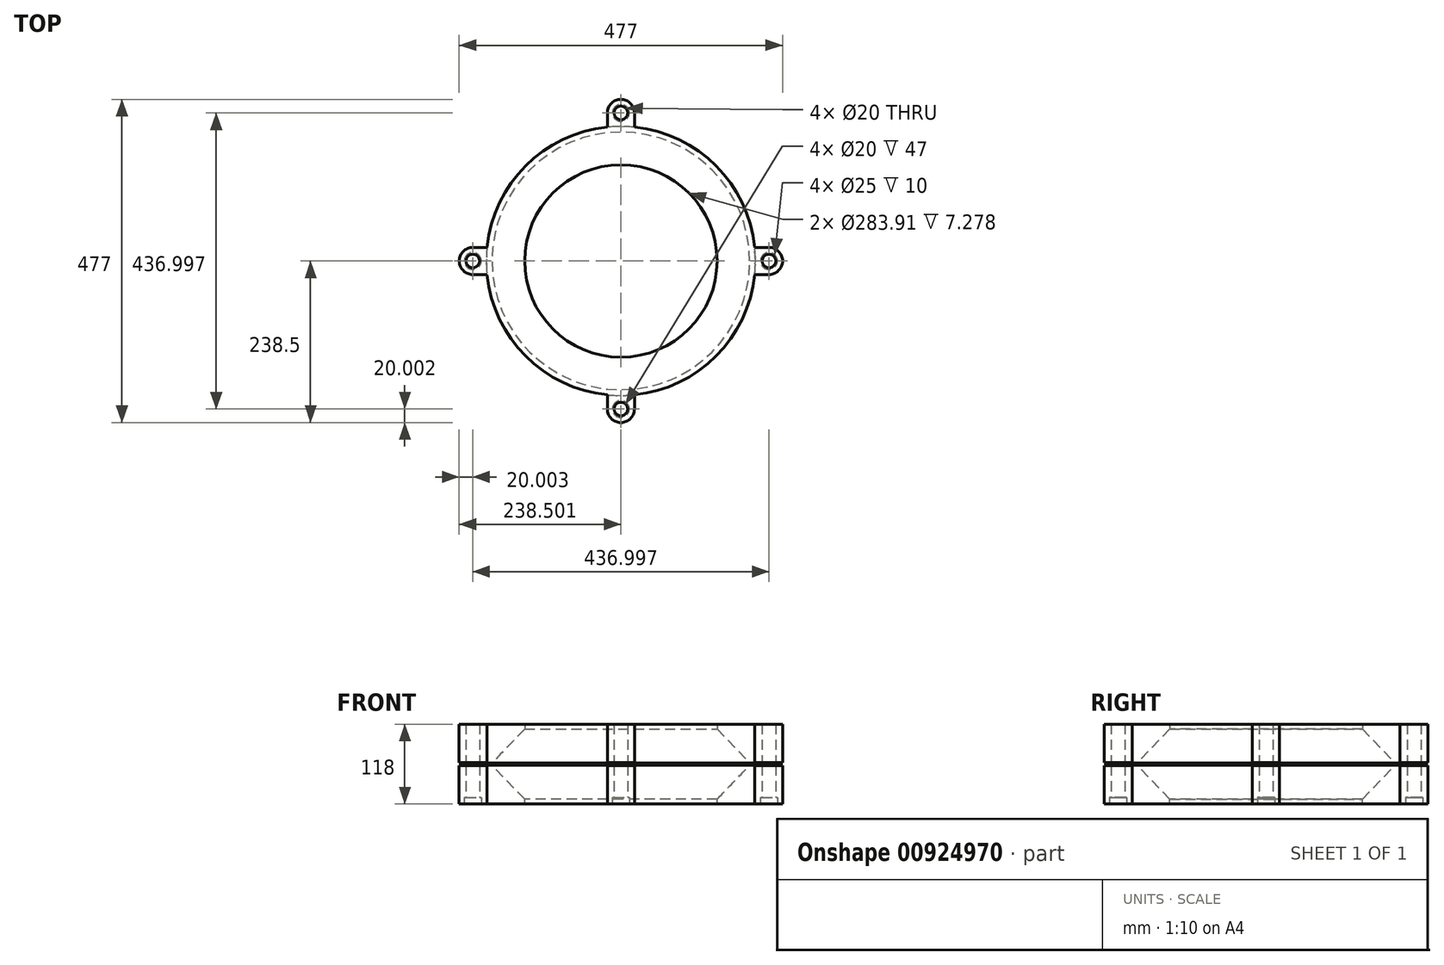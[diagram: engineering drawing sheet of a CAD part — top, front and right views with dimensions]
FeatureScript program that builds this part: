
annotation { "Feature Type Name" : "Feature", "Feature Type Description" : "" }
export const myFeature = defineFeature(function(context is Context, id is Id, definition is map)
    precondition{}
    {
        {
            var Q0;
            Q0=qCreatedBy(makeId("Front.planeOp"),FACE);
            var sketch = newSketch(context, id + "F0", { "sketchPlane" : qUnion([Q0])});
            skLineSegment(sketch, "E0", {"start": v(-122.7, 61.49) * mm, "end": v(-122.7, 4.01) * mm});
            skLineSegment(sketch, "E1", {"start": v(-122.7, 4.01) * mm, "end": v(-66.15, 4.01) * mm});
            skLineSegment(sketch, "E2", {"start": v(-66.15, 4.01) * mm, "end": v(-66.15, 11.29) * mm});
            skLineSegment(sketch, "E3", {"start": v(-66.15, 11.29) * mm, "end": v(-114.3, 61.49) * mm});
            skLineSegment(sketch, "E4", {"start": v(-114.3, 61.49) * mm, "end": v(-122.7, 61.49) * mm});
            skLineSegment(sketch, "E5", {"start": v(-122.7, 61.67) * mm, "end": v(-114.3, 61.67) * mm});
            skLineSegment(sketch, "E6.MirrorCS", {"start": v(-114.3, 61.84) * mm, "end": v(-122.7, 61.84) * mm});
            skLineSegment(sketch, "E7.MirrorCS", {"start": v(-122.7, 61.84) * mm, "end": v(-122.7, 119.32) * mm});
            skLineSegment(sketch, "E8.MirrorCS", {"start": v(-66.15, 112.04) * mm, "end": v(-114.3, 61.84) * mm});
            skLineSegment(sketch, "E9.MirrorCS", {"start": v(-122.7, 119.32) * mm, "end": v(-66.15, 119.32) * mm});
            skLineSegment(sketch, "E10.MirrorCS", {"start": v(-66.15, 119.32) * mm, "end": v(-66.15, 112.04) * mm});
            skLineSegment(sketch, "E11", {"start": v(75.8, 4.01) * mm, "end": v(75.8, 119.32) * mm});
            skSolve(sketch);
        }
        {
            var Q0;
            Q0=makeQuery(id+"F0.imprint","IMPRINT",FACE,{"disambiguationData":[TD([[makeQuery(id+"F0.imprint","IMPRINT",EDGE,{"derivedFrom":sQuery(id+"F0.wireOp",EDGE,"E6.MirrorCS")}),-1.0]])]});
            var Q1;
            Q1=makeQuery(id+"F0.imprint","IMPRINT",FACE,{"disambiguationData":[TD([[makeQuery(id+"F0.imprint","IMPRINT",EDGE,{"derivedFrom":sQuery(id+"F0.wireOp",EDGE,"E0")}),1.0]])]});
            var Q2;
            Q2=sQuery(id+"F0.wireOp",EDGE,"E11");
            revolve(context, id + "F1", {"surfaceOperationType" : NewSurfaceOperationType.NEW, "entities" : qUnion([Q0, Q1]), "axis" : qUnion([Q2]), "revolveType" : RevolveType.FULL});
        }
        {
            var Q0;
            Q0=makeQuery(id+"F1.opRevolve","SWEPT_FACE",FACE,{"disambiguationData":[OSD([sQuery(id+"F0.wireOp",EDGE,"E9.MirrorCS")])]});
            var sketch = newSketch(context, id + "F2", { "sketchPlane" : qUnion([Q0])});
            skLineSegment(sketch, "E12", {"start": v(75.8, 0) * mm, "end": v(75.8, 198.5) * mm});
            skLineSegment(sketch, "E13", {"start": v(75.8, 0) * mm, "end": v(274.3, 0) * mm});
            skLineSegment(sketch, "E14", {"start": v(75.8, 198.5) * mm, "end": v(75.8, 238.5) * mm});
            skLineSegment(sketch, "E15", {"start": v(274.3, 0) * mm, "end": v(314.3, 0) * mm});
            skLineSegment(sketch, "E16", {"start": v(75.8, 0) * mm, "end": v(75.8, -238.5) * mm});
            skLineSegment(sketch, "E17", {"start": v(75.8, 0) * mm, "end": v(-162.7, 0) * mm});
            skLineSegment(sketch, "E18.bottom", {"start": v(55.8, 238.5) * mm, "end": v(75.8, 238.5) * mm});
            skLineSegment(sketch, "E18.top", {"start": v(55.8, -238.5) * mm, "end": v(75.8, -238.5) * mm});
            skLineSegment(sketch, "E18.left", {"start": v(55.8, 238.5) * mm, "end": v(55.8, -238.5) * mm});
            skLineSegment(sketch, "E18.right", {"start": v(75.8, 238.5) * mm, "end": v(75.8, -238.5) * mm});
            skLineSegment(sketch, "E19.bottom", {"start": v(75.8, 238.5) * mm, "end": v(95.8, 238.5) * mm});
            skLineSegment(sketch, "E19.top", {"start": v(75.8, -238.5) * mm, "end": v(95.8, -238.5) * mm});
            skLineSegment(sketch, "E19.right", {"start": v(95.8, 238.5) * mm, "end": v(95.8, -238.5) * mm});
            skLineSegment(sketch, "E20.bottom", {"start": v(-162.7, 0) * mm, "end": v(314.3, 0) * mm});
            skLineSegment(sketch, "E20.top", {"start": v(-162.7, 20) * mm, "end": v(314.3, 20) * mm});
            skLineSegment(sketch, "E20.left", {"start": v(-162.7, 0) * mm, "end": v(-162.7, 20) * mm});
            skLineSegment(sketch, "E20.right", {"start": v(314.3, 0) * mm, "end": v(314.3, 20) * mm});
            skLineSegment(sketch, "E21.top", {"start": v(-162.7, -20) * mm, "end": v(314.3, -20) * mm});
            skLineSegment(sketch, "E21.left", {"start": v(-162.7, 0) * mm, "end": v(-162.7, -20) * mm});
            skLineSegment(sketch, "E21.right", {"start": v(314.3, 0) * mm, "end": v(314.3, -20) * mm});
            skSolve(sketch);
        }
        {
            var Q0;
            {var subQ0=sQuery(id+"F2.wireOp",EDGE,"E21.left");Q0=makeQuery(id+"F2.imprint","IMPRINT",FACE,{"disambiguationData":[TD([[makeQuery(id+"F2.imprint","IMPRINT",EDGE,{"derivedFrom":subQ0}),1.0]])]});}
            var Q1;
            {var subQ0=sQuery(id+"F2.wireOp",EDGE,"E20.left");Q1=makeQuery(id+"F2.imprint","IMPRINT",FACE,{"disambiguationData":[TD([[makeQuery(id+"F2.imprint","IMPRINT",EDGE,{"derivedFrom":subQ0}),-1.0]])]});}
            var Q2;
            {var subQ0=sQuery(id+"F2.wireOp",EDGE,"E18.bottom");Q2=makeQuery(id+"F2.imprint","IMPRINT",FACE,{"disambiguationData":[TD([[makeQuery(id+"F2.imprint","IMPRINT",EDGE,{"derivedFrom":subQ0}),-1.0]])]});}
            var Q3;
            {var subQ0=sQuery(id+"F2.wireOp",EDGE,"E19.bottom");Q3=makeQuery(id+"F2.imprint","IMPRINT",FACE,{"disambiguationData":[TD([[makeQuery(id+"F2.imprint","IMPRINT",EDGE,{"derivedFrom":subQ0}),-1.0]])]});}
            var Q4;
            {var subQ0=sQuery(id+"F2.wireOp",EDGE,"E18.top");Q4=makeQuery(id+"F2.imprint","IMPRINT",FACE,{"disambiguationData":[TD([[makeQuery(id+"F2.imprint","IMPRINT",EDGE,{"derivedFrom":subQ0}),1.0]])]});}
            var Q5;
            {var subQ0=sQuery(id+"F2.wireOp",EDGE,"E19.top");Q5=makeQuery(id+"F2.imprint","IMPRINT",FACE,{"disambiguationData":[TD([[makeQuery(id+"F2.imprint","IMPRINT",EDGE,{"derivedFrom":subQ0}),1.0]])]});}
            var Q6;
            {var subQ0=sQuery(id+"F2.wireOp",EDGE,"E21.right");Q6=makeQuery(id+"F2.imprint","IMPRINT",FACE,{"disambiguationData":[TD([[makeQuery(id+"F2.imprint","IMPRINT",EDGE,{"derivedFrom":subQ0}),-1.0]])]});}
            var Q7;
            {var subQ0=sQuery(id+"F2.wireOp",EDGE,"E20.right");Q7=makeQuery(id+"F2.imprint","IMPRINT",FACE,{"disambiguationData":[TD([[makeQuery(id+"F2.imprint","IMPRINT",EDGE,{"derivedFrom":subQ0}),1.0]])]});}
            extrude(context, id + "F3", {"entities" : qUnion([Q0, Q1, Q2, Q3, Q4, Q5, Q6, Q7]), "operationType" : NewBodyOperationType.ADD, "oppositeDirection" : true, "depth" : 57 * mm, "offsetDistance" : 25 * mm});
        }
        {
            var Q0;
            {var subQ0=sQuery(id+"F2.wireOp",EDGE,"E19.right");var subQ1=sQuery(id+"F0.wireOp",EDGE,"E9.MirrorCS");var subQ2=sQuery(id+"F0.wireOp",EDGE,"E7.MirrorCS");Q0=makeQuery(id+"F3.opExtrude","SWEPT_EDGE",EDGE,{"disambiguationData":[OSD([subQ2,subQ1,subQ0]),TDD([makeQuery(id+"F2.imprint","INTERSECT",VERTEX,{"disambiguationData":[OD(1.0)],"derivedFrom":[makeQuery(id+"F1.opRevolve","SWEPT_EDGE",EDGE,{"disambiguationData":[OSD([subQ2,subQ1])]}),subQ0]})])]});}
            var Q1;
            {var subQ0=sQuery(id+"F2.wireOp",EDGE,"E18.left");var subQ1=sQuery(id+"F0.wireOp",EDGE,"E9.MirrorCS");var subQ2=sQuery(id+"F0.wireOp",EDGE,"E7.MirrorCS");Q1=makeQuery(id+"F3.opExtrude","SWEPT_EDGE",EDGE,{"disambiguationData":[OSD([subQ2,subQ1,subQ0]),TDD([makeQuery(id+"F2.imprint","INTERSECT",VERTEX,{"disambiguationData":[OD(1.0)],"derivedFrom":[makeQuery(id+"F1.opRevolve","SWEPT_EDGE",EDGE,{"disambiguationData":[OSD([subQ2,subQ1])]}),subQ0]})])]});}
            var Q2;
            {var subQ0=sQuery(id+"F2.wireOp",EDGE,"E21.top");var subQ1=sQuery(id+"F0.wireOp",EDGE,"E9.MirrorCS");var subQ2=sQuery(id+"F0.wireOp",EDGE,"E7.MirrorCS");Q2=makeQuery(id+"F3.opExtrude","SWEPT_EDGE",EDGE,{"disambiguationData":[OSD([subQ2,subQ1,subQ0]),TDD([makeQuery(id+"F2.imprint","INTERSECT",VERTEX,{"disambiguationData":[OD(1.0)],"derivedFrom":[makeQuery(id+"F1.opRevolve","SWEPT_EDGE",EDGE,{"disambiguationData":[OSD([subQ2,subQ1])]}),subQ0]})])]});}
            var Q3;
            {var subQ0=sQuery(id+"F2.wireOp",EDGE,"E20.top");var subQ1=sQuery(id+"F0.wireOp",EDGE,"E9.MirrorCS");var subQ2=sQuery(id+"F0.wireOp",EDGE,"E7.MirrorCS");Q3=makeQuery(id+"F3.opExtrude","SWEPT_EDGE",EDGE,{"disambiguationData":[OSD([subQ2,subQ1,subQ0]),TDD([makeQuery(id+"F2.imprint","INTERSECT",VERTEX,{"disambiguationData":[OD(1.0)],"derivedFrom":[makeQuery(id+"F1.opRevolve","SWEPT_EDGE",EDGE,{"disambiguationData":[OSD([subQ2,subQ1])]}),subQ0]})])]});}
            var Q4;
            {var subQ0=sQuery(id+"F2.wireOp",EDGE,"E19.right");var subQ1=sQuery(id+"F0.wireOp",EDGE,"E9.MirrorCS");var subQ2=sQuery(id+"F0.wireOp",EDGE,"E7.MirrorCS");Q4=makeQuery(id+"F3.opExtrude","SWEPT_EDGE",EDGE,{"disambiguationData":[OSD([subQ2,subQ1,subQ0]),TDD([makeQuery(id+"F2.imprint","INTERSECT",VERTEX,{"disambiguationData":[OD(0.0)],"derivedFrom":[makeQuery(id+"F1.opRevolve","SWEPT_EDGE",EDGE,{"disambiguationData":[OSD([subQ2,subQ1])]}),subQ0]})])]});}
            var Q5;
            {var subQ0=sQuery(id+"F2.wireOp",EDGE,"E18.left");var subQ1=sQuery(id+"F0.wireOp",EDGE,"E9.MirrorCS");var subQ2=sQuery(id+"F0.wireOp",EDGE,"E7.MirrorCS");Q5=makeQuery(id+"F3.opExtrude","SWEPT_EDGE",EDGE,{"disambiguationData":[OSD([subQ2,subQ1,subQ0]),TDD([makeQuery(id+"F2.imprint","INTERSECT",VERTEX,{"disambiguationData":[OD(0.0)],"derivedFrom":[makeQuery(id+"F1.opRevolve","SWEPT_EDGE",EDGE,{"disambiguationData":[OSD([subQ2,subQ1])]}),subQ0]})])]});}
            var Q6;
            {var subQ0=sQuery(id+"F2.wireOp",EDGE,"E20.top");var subQ1=sQuery(id+"F0.wireOp",EDGE,"E9.MirrorCS");var subQ2=sQuery(id+"F0.wireOp",EDGE,"E7.MirrorCS");Q6=makeQuery(id+"F3.opExtrude","SWEPT_EDGE",EDGE,{"disambiguationData":[OSD([subQ2,subQ1,subQ0]),TDD([makeQuery(id+"F2.imprint","INTERSECT",VERTEX,{"disambiguationData":[OD(0.0)],"derivedFrom":[makeQuery(id+"F1.opRevolve","SWEPT_EDGE",EDGE,{"disambiguationData":[OSD([subQ2,subQ1])]}),subQ0]})])]});}
            var Q7;
            {var subQ0=sQuery(id+"F2.wireOp",EDGE,"E21.top");var subQ1=sQuery(id+"F0.wireOp",EDGE,"E9.MirrorCS");var subQ2=sQuery(id+"F0.wireOp",EDGE,"E7.MirrorCS");Q7=makeQuery(id+"F3.opExtrude","SWEPT_EDGE",EDGE,{"disambiguationData":[OSD([subQ2,subQ1,subQ0]),TDD([makeQuery(id+"F2.imprint","INTERSECT",VERTEX,{"disambiguationData":[OD(0.0)],"derivedFrom":[makeQuery(id+"F1.opRevolve","SWEPT_EDGE",EDGE,{"disambiguationData":[OSD([subQ2,subQ1])]}),subQ0]})])]});}
            var Q8;
            Q8=makeQuery(id+"F3.opExtrude","SWEPT_EDGE",EDGE,{"disambiguationData":[OSD([sQuery(id+"F2.wireOp",EDGE,"E21.top"),sQuery(id+"F2.wireOp",EDGE,"E21.left")])]});
            var Q9;
            Q9=makeQuery(id+"F3.opExtrude","SWEPT_EDGE",EDGE,{"disambiguationData":[OSD([sQuery(id+"F2.wireOp",EDGE,"E20.top"),sQuery(id+"F2.wireOp",EDGE,"E20.left")])]});
            var Q10;
            Q10=makeQuery(id+"F3.opExtrude","SWEPT_EDGE",EDGE,{"disambiguationData":[OSD([sQuery(id+"F2.wireOp",EDGE,"E18.bottom"),sQuery(id+"F2.wireOp",EDGE,"E18.left")])]});
            var Q11;
            Q11=makeQuery(id+"F3.opExtrude","SWEPT_EDGE",EDGE,{"disambiguationData":[OSD([sQuery(id+"F2.wireOp",EDGE,"E19.bottom"),sQuery(id+"F2.wireOp",EDGE,"E19.right")])]});
            var Q12;
            Q12=makeQuery(id+"F3.opExtrude","SWEPT_EDGE",EDGE,{"disambiguationData":[OSD([sQuery(id+"F2.wireOp",EDGE,"E20.top"),sQuery(id+"F2.wireOp",EDGE,"E20.right")])]});
            var Q13;
            Q13=makeQuery(id+"F3.opExtrude","SWEPT_EDGE",EDGE,{"disambiguationData":[OSD([sQuery(id+"F2.wireOp",EDGE,"E21.top"),sQuery(id+"F2.wireOp",EDGE,"E21.right")])]});
            var Q14;
            Q14=makeQuery(id+"F3.opExtrude","SWEPT_EDGE",EDGE,{"disambiguationData":[OSD([sQuery(id+"F2.wireOp",EDGE,"E19.top"),sQuery(id+"F2.wireOp",EDGE,"E19.right")])]});
            var Q15;
            Q15=makeQuery(id+"F3.opExtrude","SWEPT_EDGE",EDGE,{"disambiguationData":[OSD([sQuery(id+"F2.wireOp",EDGE,"E18.top"),sQuery(id+"F2.wireOp",EDGE,"E18.left")])]});
            fillet(context, id + "F4", {"entities" : qUnion([Q0, Q1, Q2, Q3, Q4, Q5, Q6, Q7, Q8, Q9, Q10, Q11, Q12, Q13, Q14, Q15]), "radius" : 20 * mm, "tangentPropagation" : true, "allowEdgeOverflow" : false});
        }
        {
            var Q0;
            Q0=makeQuery(id+"F1.opRevolve","SWEPT_BODY",BODY,{"disambiguationData":[OSD([sQuery(id+"F0.wireOp",EDGE,"E0"),sQuery(id+"F0.wireOp",EDGE,"E1"),sQuery(id+"F0.wireOp",EDGE,"E2"),sQuery(id+"F0.wireOp",EDGE,"E3"),sQuery(id+"F0.wireOp",EDGE,"E4")])]});
            deleteBodies(context, id + "F5", {"entities" : qUnion([Q0])});
        }
        {
            var Q0;
            Q0=makeQuery(id+"F1.opRevolve","SWEPT_BODY",BODY,{"disambiguationData":[OSD([sQuery(id+"F0.wireOp",EDGE,"E6.MirrorCS"),sQuery(id+"F0.wireOp",EDGE,"E7.MirrorCS"),sQuery(id+"F0.wireOp",EDGE,"E8.MirrorCS"),sQuery(id+"F0.wireOp",EDGE,"E9.MirrorCS"),sQuery(id+"F0.wireOp",EDGE,"E10.MirrorCS")])]});
            transform(context, id + "F6", {"entities" : qUnion([Q0]), "transformType" : TransformType.TRANSLATION_3D, "dx" : 0 * mm, "dy" : 0 * mm, "dz" : -59 * mm, "makeCopy" : true});
        }
        {
            var Q0;
            Q0=makeQuery(id+"F1.opRevolve","SWEPT_BODY",BODY,{"disambiguationData":[OSD([sQuery(id+"F0.wireOp",EDGE,"E6.MirrorCS"),sQuery(id+"F0.wireOp",EDGE,"E7.MirrorCS"),sQuery(id+"F0.wireOp",EDGE,"E8.MirrorCS"),sQuery(id+"F0.wireOp",EDGE,"E9.MirrorCS"),sQuery(id+"F0.wireOp",EDGE,"E10.MirrorCS")])]});
            var Q1;
            Q1=sQuery(id+"F2.wireOp",EDGE,"E18.right");
            transform(context, id + "F7", {"entities" : qUnion([Q0]), "transformType" : TransformType.ROTATION, "transformAxis" : qUnion([Q1]), "angle" : 180 * degree, "makeCopy" : false});
        }
        {
            var Q0;
            Q0=makeQuery(id+"F1.opRevolve","SWEPT_BODY",BODY,{"disambiguationData":[OSD([sQuery(id+"F0.wireOp",EDGE,"E6.MirrorCS"),sQuery(id+"F0.wireOp",EDGE,"E7.MirrorCS"),sQuery(id+"F0.wireOp",EDGE,"E8.MirrorCS"),sQuery(id+"F0.wireOp",EDGE,"E9.MirrorCS"),sQuery(id+"F0.wireOp",EDGE,"E10.MirrorCS")])]});
            transform(context, id + "F8", {"entities" : qUnion([Q0]), "transformType" : TransformType.TRANSLATION_3D, "dx" : 0 * mm, "dy" : 0 * mm, "dz" : -177 * mm, "makeCopy" : false});
        }
        {
            var Q0;
            {var subQ0=sQuery(id+"F2.wireOp",EDGE,"E21.top");var subQ1=sQuery(id+"F2.wireOp",EDGE,"E20.top");var subQ2=sQuery(id+"F0.wireOp",EDGE,"E9.MirrorCS");var subQ3=sQuery(id+"F0.wireOp",EDGE,"E7.MirrorCS");var subQ4=sQuery(id+"F2.wireOp",EDGE,"E19.right");var subQ5=sQuery(id+"F2.wireOp",EDGE,"E18.left");Q0=makeQuery(id+"F3.boolean.opBoolean","MERGE",FACE,{"derivedFrom":[makeQuery(id+"F1.opRevolve","SWEPT_FACE",FACE,{"disambiguationData":[OSD([subQ2])]}),makeQuery(id+"F3.opExtrude","CAP_FACE",FACE,{"disambiguationData":[OSD([subQ3,subQ2,sQuery(id+"F2.wireOp",EDGE,"E18.bottom"),subQ5,sQuery(id+"F2.wireOp",EDGE,"E19.bottom"),subQ4])],"isStart":true}),makeQuery(id+"F3.opExtrude","CAP_FACE",FACE,{"disambiguationData":[OSD([subQ3,subQ2,sQuery(id+"F2.wireOp",EDGE,"E18.top"),subQ5,sQuery(id+"F2.wireOp",EDGE,"E19.top"),subQ4])],"isStart":true}),makeQuery(id+"F3.opExtrude","CAP_FACE",FACE,{"disambiguationData":[OSD([subQ3,subQ2,subQ1,sQuery(id+"F2.wireOp",EDGE,"E20.left"),subQ0,sQuery(id+"F2.wireOp",EDGE,"E21.left")])],"isStart":true}),makeQuery(id+"F3.opExtrude","CAP_FACE",FACE,{"disambiguationData":[OSD([subQ3,subQ2,subQ1,sQuery(id+"F2.wireOp",EDGE,"E20.right"),subQ0,sQuery(id+"F2.wireOp",EDGE,"E21.right")])],"isStart":true})]});}
            var sketch = newSketch(context, id + "F9", { "sketchPlane" : qUnion([Q0])});
            skPoint(sketch, "E22", {"position": v(75.8, 218.5) * mm});
            skPoint(sketch, "E23", {"position": v(294.3, 0) * mm});
            skPoint(sketch, "E24", {"position": v(75.8, -218.5) * mm});
            skPoint(sketch, "E25", {"position": v(-142.7, 0) * mm});
            skSolve(sketch);
        }
        {
            var Q0;
            Q0=sQuery(id+"F9.wireOp",VERTEX,"E22");
            var Q1;
            Q1=sQuery(id+"F9.wireOp",VERTEX,"E25");
            var Q2;
            Q2=sQuery(id+"F9.wireOp",VERTEX,"E24");
            var Q3;
            Q3=sQuery(id+"F9.wireOp",VERTEX,"E23");
            var Q4;
            Q4=makeQuery(id+"F1.opRevolve","SWEPT_BODY",BODY,{"disambiguationData":[OSD([sQuery(id+"F0.wireOp",EDGE,"E6.MirrorCS"),sQuery(id+"F0.wireOp",EDGE,"E7.MirrorCS"),sQuery(id+"F0.wireOp",EDGE,"E8.MirrorCS"),sQuery(id+"F0.wireOp",EDGE,"E9.MirrorCS"),sQuery(id+"F0.wireOp",EDGE,"E10.MirrorCS")])]});
            var Q5;
            Q5=makeQuery(id+"F6.opPattern","COPY",BODY,{"derivedFrom":makeQuery(id+"F1.opRevolve","SWEPT_BODY",BODY,{"disambiguationData":[OSD([sQuery(id+"F0.wireOp",EDGE,"E6.MirrorCS"),sQuery(id+"F0.wireOp",EDGE,"E7.MirrorCS"),sQuery(id+"F0.wireOp",EDGE,"E8.MirrorCS"),sQuery(id+"F0.wireOp",EDGE,"E9.MirrorCS"),sQuery(id+"F0.wireOp",EDGE,"E10.MirrorCS")])]}),"instanceName":"1"});
            hole(context, id + "F10", {"style" : HoleStyle.C_BORE, "endStyle" : HoleEndStyle.THROUGH, "holeDiameter" : 20 * mm, "cBoreDiameter" : 25 * mm, "cBoreDepth" : 10 * mm, "majorDiameter" : 5 * mm, "isTappedThrough" : true, "tappedDepth" : 12 * mm, "tapClearance" : 3, "locations" : qUnion([Q0, Q1, Q2, Q3]), "scope" : qUnion([Q4, Q5])});
        }
    });
